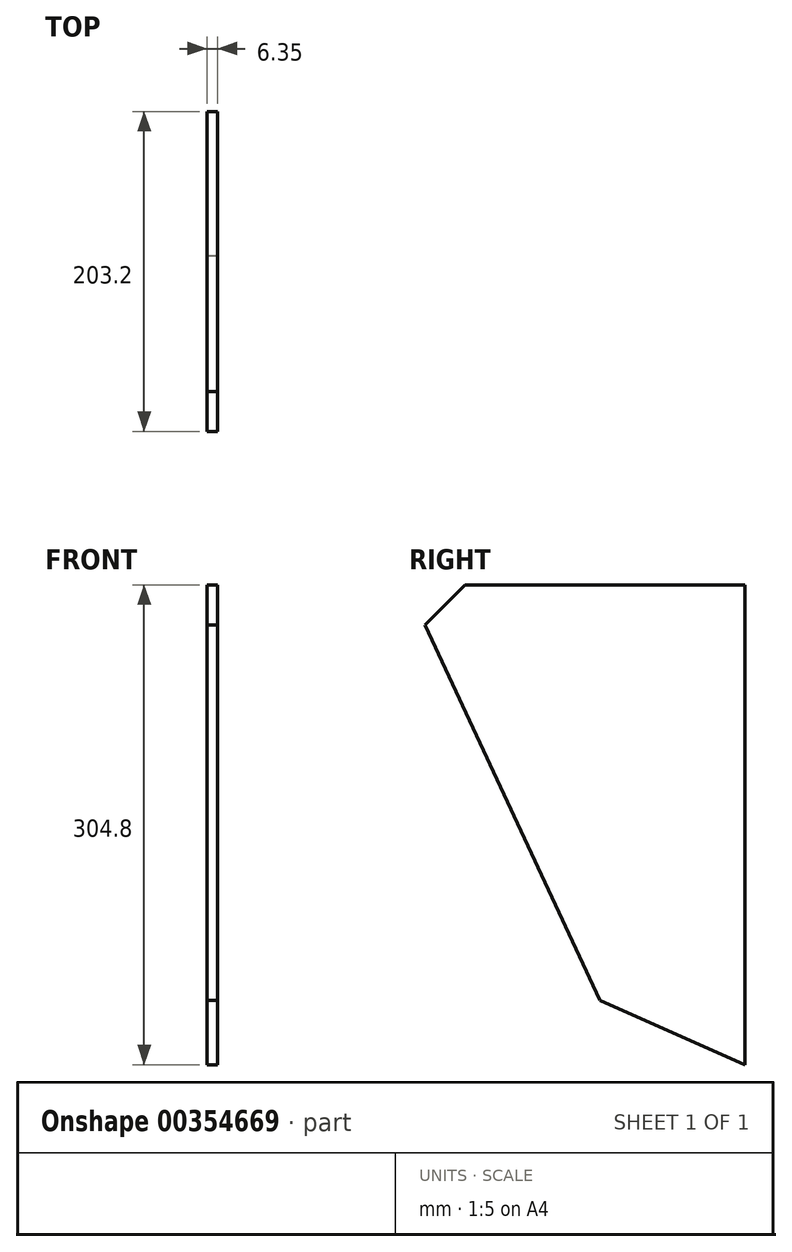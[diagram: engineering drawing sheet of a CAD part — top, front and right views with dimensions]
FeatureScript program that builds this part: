
annotation { "Feature Type Name" : "Feature", "Feature Type Description" : "" }
export const myFeature = defineFeature(function(context is Context, id is Id, definition is map)
    precondition{}
    {
        {
            var Q0;
            Q0=qCreatedBy(makeId("Right.planeOp"),FACE);
            var sketch = newSketch(context, id + "F0", { "sketchPlane" : qUnion([Q0])});
            skLineSegment(sketch, "E0.bottom", {"start": v(101.6, 152.4) * mm, "end": v(-76.2, 152.4) * mm});
            skLineSegment(sketch, "E0.left", {"start": v(101.6, 152.4) * mm, "end": v(101.6, -152.4) * mm});
            skPoint(sketch, "E0.middle", {"position": v(0, 0) * mm});
            skLineSegment(sketch, "E1", {"start": v(-101.6, 127) * mm, "end": v(-76.2, 152.4) * mm});
            skPoint(sketch, "E2.orphan", {"position": v(-101.6, 152.4) * mm});
            skLineSegment(sketch, "E3", {"start": v(-101.6, 127) * mm, "end": v(9.58, -111.43) * mm});
            skLineSegment(sketch, "E4", {"start": v(9.58, -111.43) * mm, "end": v(101.6, -152.4) * mm});
            skPoint(sketch, "E0.top.end.orphan", {"position": v(-101.6, -152.4) * mm});
            skSolve(sketch);
        }
        {
            var Q0;
            Q0=qSketchRegion(id+"F0",true);
            extrude(context, id + "F1", {"entities" : qUnion([Q0]), "depth" : 6.35 * mm});
        }
    });
